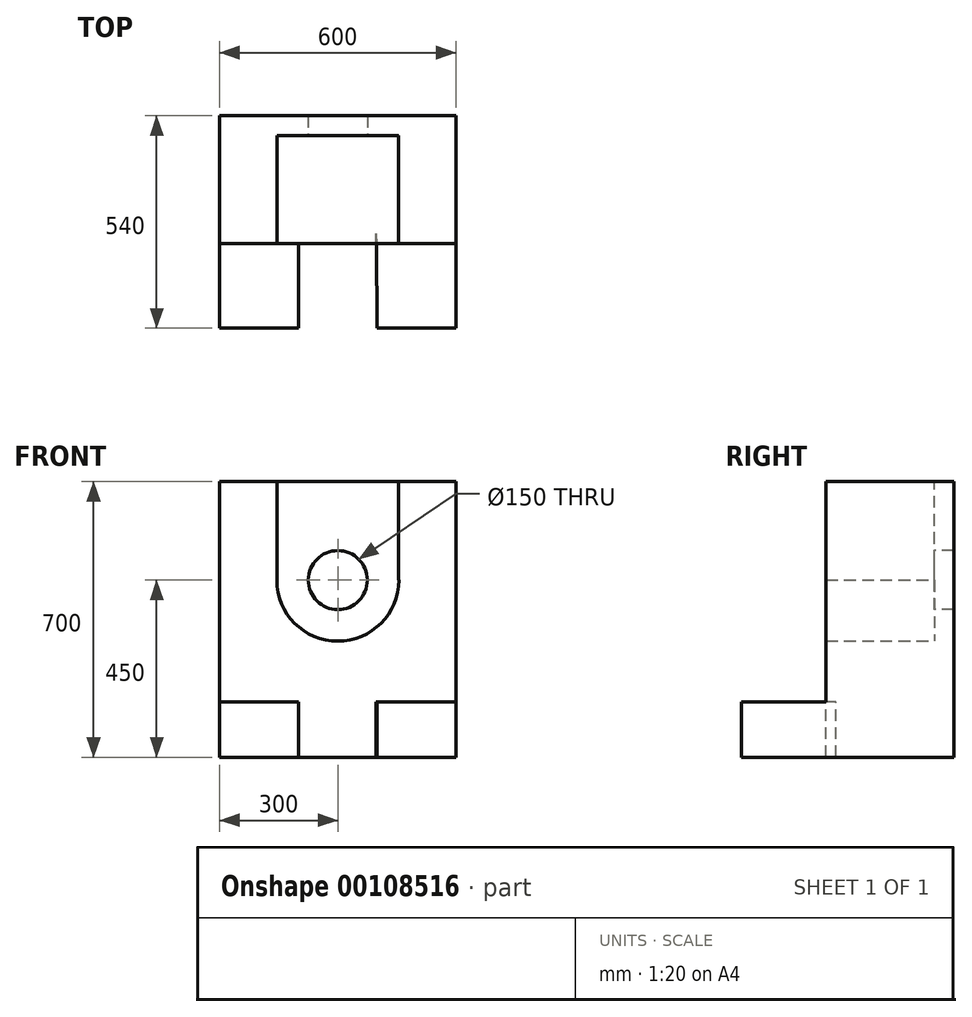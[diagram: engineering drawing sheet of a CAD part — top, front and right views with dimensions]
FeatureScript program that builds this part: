
annotation { "Feature Type Name" : "Feature", "Feature Type Description" : "" }
export const myFeature = defineFeature(function(context is Context, id is Id, definition is map)
    precondition{}
    {
        {
            var Q0;
            Q0=qCreatedBy(makeId("Front.planeOp"),FACE);
            var sketch = newSketch(context, id + "F0", { "sketchPlane" : qUnion([Q0])});
            skLineSegment(sketch, "E0.bottom", {"start": v(300, 350) * mm, "end": v(-300, 350) * mm});
            skLineSegment(sketch, "E0.top", {"start": v(300, -350) * mm, "end": v(-300, -350) * mm});
            skLineSegment(sketch, "E0.left", {"start": v(300, 350) * mm, "end": v(300, -350) * mm});
            skLineSegment(sketch, "E0.right", {"start": v(-300, 350) * mm, "end": v(-300, -350) * mm});
            skPoint(sketch, "E0.middle", {"position": v(0, 0) * mm});
            skSolve(sketch);
        }
        {
            var Q0;
            Q0 = qSketchRegion(id + "F0", true);
            extrude(context, id + "F1", {"entities" : qUnion([Q0]), "depth" : 540 * mm});
        }
        {
            var Q0;
            Q0=makeQuery(id+"F1.opExtrude","CAP_FACE",FACE,{"disambiguationData":[OSD([sQuery(id+"F0.wireOp",EDGE,"E0.bottom"),sQuery(id+"F0.wireOp",EDGE,"E0.top"),sQuery(id+"F0.wireOp",EDGE,"E0.left"),sQuery(id+"F0.wireOp",EDGE,"E0.right")])],"isStart":false});
            var sketch = newSketch(context, id + "F2", { "sketchPlane" : qUnion([Q0])});
            skLineSegment(sketch, "E1.bottom", {"start": v(-300, 350) * mm, "end": v(300, 350) * mm});
            skLineSegment(sketch, "E1.top", {"start": v(-300, -210) * mm, "end": v(300, -210) * mm});
            skLineSegment(sketch, "E1.left", {"start": v(-300, 350) * mm, "end": v(-300, -210) * mm});
            skLineSegment(sketch, "E1.right", {"start": v(300, 350) * mm, "end": v(300, -210) * mm});
            skSolve(sketch);
        }
        {
            var Q0;
            Q0 = qSketchRegion(id + "F2", true);
            extrude(context, id + "F3", {"entities" : qUnion([Q0]), "operationType" : NewBodyOperationType.REMOVE, "oppositeDirection" : true, "depth" : 240 * mm});
        }
        {
            var Q0;
            Q0=makeQuery(id+"F3.boolean.opBoolean","COPY",FACE,{"derivedFrom":makeQuery(id+"F3.opExtrude","SWEPT_FACE",FACE,{"disambiguationData":[OSD([sQuery(id+"F2.wireOp",EDGE,"E1.top")])]})});
            var sketch = newSketch(context, id + "F4", { "sketchPlane" : qUnion([Q0])});
            skLineSegment(sketch, "E2.bottom", {"start": v(-300, -540) * mm, "end": v(-100, -540) * mm});
            skLineSegment(sketch, "E2.top", {"start": v(-100, -300) * mm, "end": v(97.49, -300) * mm});
            skLineSegment(sketch, "E3", {"start": v(-100, -540) * mm, "end": v(100, -540) * mm});
            skLineSegment(sketch, "E4", {"start": v(-100, -540) * mm, "end": v(-100, -300) * mm});
            skLineSegment(sketch, "E5", {"start": v(97.49, -300) * mm, "end": v(100, -540) * mm});
            skSolve(sketch);
        }
        {
            var Q0;
            Q0 = qSketchRegion(id + "F4", true);
            extrude(context, id + "F5", {"entities" : qUnion([Q0]), "operationType" : NewBodyOperationType.REMOVE, "endBound" : BoundingType.THROUGH_ALL, "oppositeDirection" : true, "depth" : 25 * mm});
        }
        {
            var Q0;
            Q0=makeQuery(id+"F5.boolean.opBoolean","MERGE",FACE,{"derivedFrom":[makeQuery(id+"F3.boolean.opBoolean","COPY",FACE,{"derivedFrom":makeQuery(id+"F3.opExtrude","CAP_FACE",FACE,{"disambiguationData":[OSD([sQuery(id+"F2.wireOp",EDGE,"E1.bottom"),sQuery(id+"F2.wireOp",EDGE,"E1.top"),sQuery(id+"F2.wireOp",EDGE,"E1.left"),sQuery(id+"F2.wireOp",EDGE,"E1.right")])],"isStart":false})}),makeQuery(id+"F5.opExtrude","SWEPT_FACE",FACE,{"disambiguationData":[OSD([sQuery(id+"F4.wireOp",EDGE,"E2.top")])]})]});
            var sketch = newSketch(context, id + "F6", { "sketchPlane" : qUnion([Q0])});
            skLineSegment(sketch, "E6.bottom", {"start": v(155, 100) * mm, "end": v(154.1, 100) * mm});
            skPoint(sketch, "E6.middle", {"position": v(0, 350) * mm});
            skPoint(sketch, "E6.right.end.orphan", {"position": v(-154.1, 600) * mm});
            skPoint(sketch, "E6.left.end.orphan", {"position": v(154.1, 600) * mm});
            skLineSegment(sketch, "E7", {"start": v(-154.1, 100) * mm, "end": v(-154.1, 350) * mm});
            skLineSegment(sketch, "E8", {"start": v(154.1, 100) * mm, "end": v(154.1, 350) * mm});
            skArc(sketch, "E9", {"start": v(-155, 100) * mm, "mid": v(0, -55) * mm, "end": v(155, 100) * mm});
            skLineSegment(sketch, "E10.trimOffspring", {"start": v(-154.1, 100) * mm, "end": v(-155, 100) * mm});
            skSolve(sketch);
        }
        {
            var Q0;
            Q0 = qSketchRegion(id + "F6", true);
            var Q1;
            Q1=makeQuery(id+"F6.imprint","IMPRINT",FACE,{"disambiguationData":[TD([[makeQuery(id+"F6.imprint","IMPRINT",EDGE,{"derivedFrom":sQuery(id+"F6.wireOp",EDGE,"E6.bottom")}),-1.0]])]});
            extrude(context, id + "F7", {"entities" : qUnion([Q0, Q1]), "operationType" : NewBodyOperationType.ADD, "depth" : 25 * mm});
        }
        {
            var Q0;
            Q0=makeQuery(id+"F5.boolean.opBoolean","MERGE",FACE,{"derivedFrom":[makeQuery(id+"F3.boolean.opBoolean","COPY",FACE,{"derivedFrom":makeQuery(id+"F3.opExtrude","CAP_FACE",FACE,{"disambiguationData":[OSD([sQuery(id+"F2.wireOp",EDGE,"E1.bottom"),sQuery(id+"F2.wireOp",EDGE,"E1.top"),sQuery(id+"F2.wireOp",EDGE,"E1.left"),sQuery(id+"F2.wireOp",EDGE,"E1.right")])],"isStart":false})}),makeQuery(id+"F5.opExtrude","SWEPT_FACE",FACE,{"disambiguationData":[OSD([sQuery(id+"F4.wireOp",EDGE,"E2.top")])]})]});
            var Q1;
            Q1=makeQuery(id+"F5.boolean.opBoolean","MERGE",FACE,{"derivedFrom":[makeQuery(id+"F3.boolean.opBoolean","COPY",FACE,{"derivedFrom":makeQuery(id+"F3.opExtrude","CAP_FACE",FACE,{"disambiguationData":[OSD([sQuery(id+"F2.wireOp",EDGE,"E1.bottom"),sQuery(id+"F2.wireOp",EDGE,"E1.top"),sQuery(id+"F2.wireOp",EDGE,"E1.left"),sQuery(id+"F2.wireOp",EDGE,"E1.right")])],"isStart":false})}),makeQuery(id+"F5.opExtrude","SWEPT_FACE",FACE,{"disambiguationData":[OSD([sQuery(id+"F4.wireOp",EDGE,"E2.top")])]})]});
            extrude(context, id + "F8", {"entities" : qUnion([Q0, Q1]), "operationType" : NewBodyOperationType.REMOVE, "oppositeDirection" : true, "depth" : 250 * mm});
        }
        {
            var Q0;
            Q0=makeQuery(id+"F8.boolean.opBoolean","COPY",FACE,{"derivedFrom":makeQuery(id+"F8.opExtrude","CAP_FACE",FACE,{"disambiguationData":[OSD([sQuery(id+"F2.wireOp",EDGE,"E1.bottom"),sQuery(id+"F2.wireOp",EDGE,"E1.top"),sQuery(id+"F2.wireOp",EDGE,"E1.left"),sQuery(id+"F2.wireOp",EDGE,"E1.right"),sQuery(id+"F4.wireOp",EDGE,"E2.top")])],"isStart":false})});
            var sketch = newSketch(context, id + "F9", { "sketchPlane" : qUnion([Q0])});
            skCircle(sketch, "E11", {"center": v(0, 100) * mm, "radius": 75 * mm});
            skSolve(sketch);
        }
        {
            var Q0;
            Q0 = qSketchRegion(id + "F9", true);
            extrude(context, id + "F10", {"entities" : qUnion([Q0]), "operationType" : NewBodyOperationType.REMOVE, "endBound" : BoundingType.THROUGH_ALL, "oppositeDirection" : true, "depth" : 25 * mm});
        }
    });
